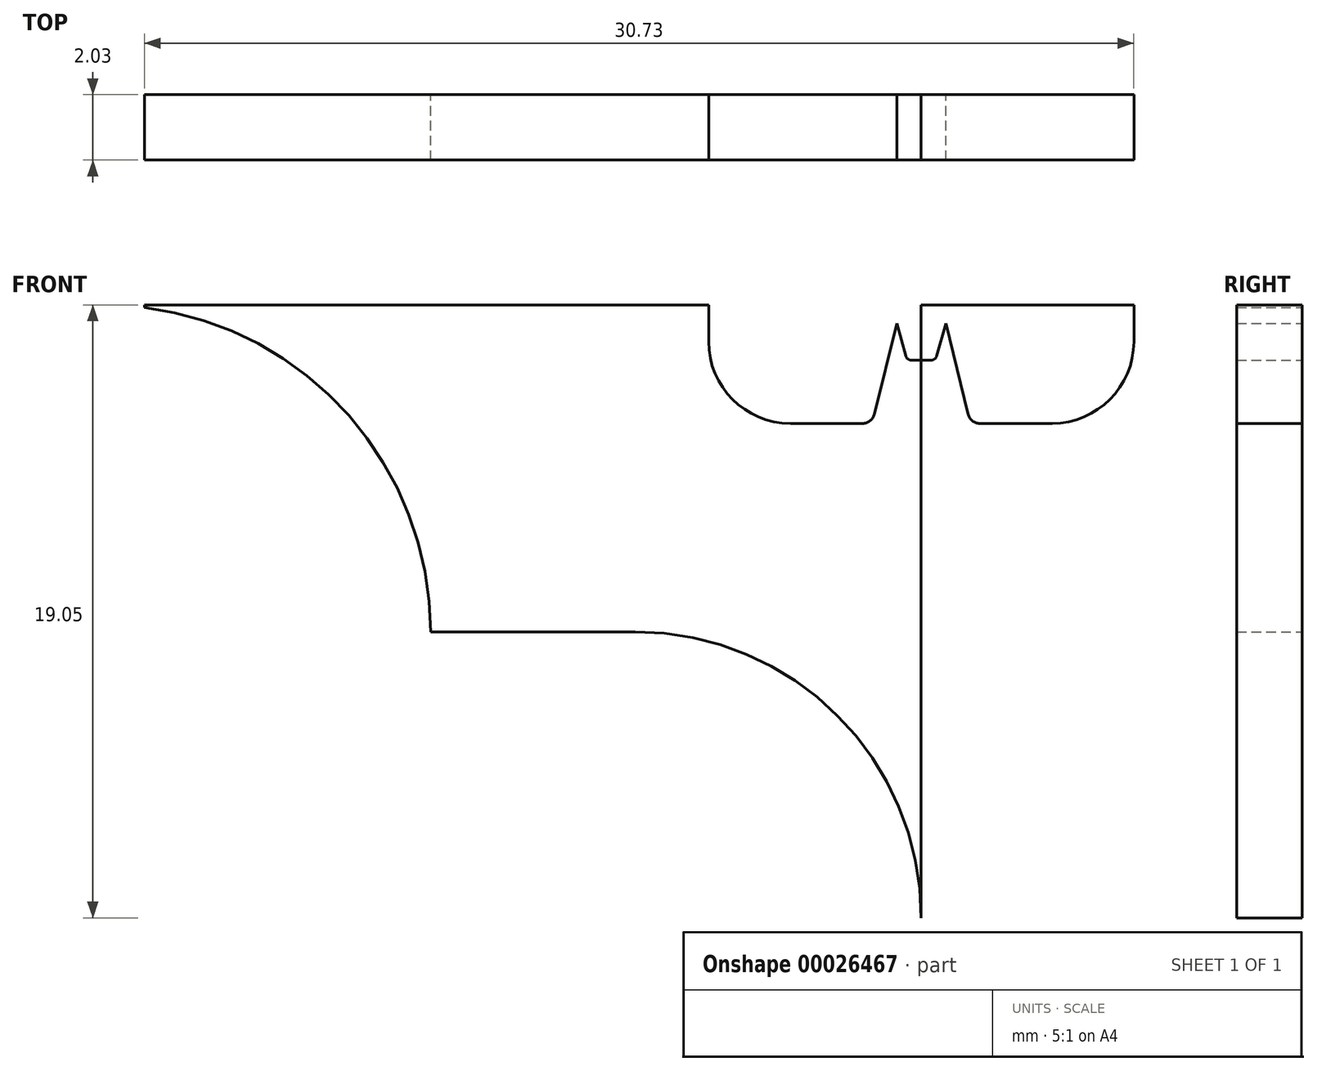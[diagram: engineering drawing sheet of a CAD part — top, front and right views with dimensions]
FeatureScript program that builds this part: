
annotation { "Feature Type Name" : "Feature", "Feature Type Description" : "" }
export const myFeature = defineFeature(function(context is Context, id is Id, definition is map)
    precondition{}
    {
        {
            var Q0;
            Q0=qCreatedBy(makeId("Front.planeOp"),FACE);
            var sketch = newSketch(context, id + "F0", { "sketchPlane" : qUnion([Q0])});
            skLineSegment(sketch, "E0", {"start": v(0, 0) * mm, "end": v(0, 50.8) * mm});
            skLineSegment(sketch, "E1.left", {"start": v(50.8, 0) * mm, "end": v(50.8, 5.14) * mm});
            skLineSegment(sketch, "E2.top", {"start": v(0, 17.78) * mm, "end": v(-1.27, 17.78) * mm});
            skLineSegment(sketch, "E2.right", {"start": v(0, 0) * mm, "end": v(0, 17.78) * mm});
            skPoint(sketch, "E3", {"position": v(0, 7.11) * mm});
            skLineSegment(sketch, "E4", {"start": v(8.9, -1.34) * mm, "end": v(8.9, 7.62) * mm});
            skPoint(sketch, "E5.newPointA", {"position": v(8.9, 9.32) * mm});
            skArc(sketch, "E5.filletArc", {"start": v(8.9, 7.62) * mm, "mid": v(5.91, 14.8) * mm, "end": v(-1.27, 17.78) * mm});
            skLineSegment(sketch, "E6", {"start": v(8.9, 7.62) * mm, "end": v(15.24, 7.62) * mm});
            skLineSegment(sketch, "E7", {"start": v(24.13, 0) * mm, "end": v(24.13, -1.27) * mm});
            skPoint(sketch, "E8.visualSharp", {"position": v(24.13, 7.62) * mm});
            skArc(sketch, "E8.filletArc", {"start": v(24.13, -1.27) * mm, "mid": v(21.53, 5.02) * mm, "end": v(15.24, 7.62) * mm});
            skLineSegment(sketch, "E9", {"start": v(-1.27, 17.78) * mm, "end": v(24.13, 17.78) * mm});
            skLineSegment(sketch, "E10", {"start": v(24.13, -1.27) * mm, "end": v(24.13, 17.78) * mm});
            skLineSegment(sketch, "E11.bottom", {"start": v(24.13, 17.78) * mm, "end": v(17.53, 17.78) * mm});
            skLineSegment(sketch, "E11.top", {"start": v(22.3, 14.1) * mm, "end": v(20.07, 14.1) * mm});
            skLineSegment(sketch, "E11.left", {"start": v(24.13, 17.78) * mm, "end": v(24.13, 14.1) * mm});
            skLineSegment(sketch, "E11.right", {"start": v(17.53, 17.78) * mm, "end": v(17.53, 16.64) * mm});
            skPoint(sketch, "E12.visualSharp", {"position": v(17.53, 14.1) * mm});
            skArc(sketch, "E12.filletArc", {"start": v(17.53, 16.64) * mm, "mid": v(18.27, 14.84) * mm, "end": v(20.07, 14.1) * mm});
            skLineSegment(sketch, "E13.bottom", {"start": v(24.13, 14.1) * mm, "end": v(22.6, 14.1) * mm});
            skLineSegment(sketch, "E13.top", {"start": v(24.13, 17.2) * mm, "end": v(22.6, 17.2) * mm, "construction": true});
            skLineSegment(sketch, "E13.left", {"start": v(24.13, 14.1) * mm, "end": v(24.13, 17.2) * mm});
            skLineSegment(sketch, "E13.right", {"start": v(22.6, 14.1) * mm, "end": v(22.6, 17.2) * mm, "construction": true});
            skLineSegment(sketch, "E14", {"start": v(22.68, 14.39) * mm, "end": v(23.37, 17.2) * mm});
            skLineSegment(sketch, "E15", {"start": v(23.37, 17.2) * mm, "end": v(23.65, 16.19) * mm});
            skLineSegment(sketch, "E16", {"start": v(23.82, 16.06) * mm, "end": v(24.13, 16.06) * mm});
            skPoint(sketch, "E17.newPointB", {"position": v(24.13, 14.1) * mm});
            skArc(sketch, "E17.filletArc", {"start": v(22.3, 14.1) * mm, "mid": v(22.54, 14.18) * mm, "end": v(22.68, 14.39) * mm});
            skPoint(sketch, "E18.visualSharp", {"position": v(23.69, 16.06) * mm});
            skArc(sketch, "E18.filletArc", {"start": v(23.65, 16.19) * mm, "mid": v(23.71, 16.1) * mm, "end": v(23.82, 16.06) * mm});
            skArc(sketch, "E19.MirrorCS", {"start": v(25.95, 14.1) * mm, "mid": v(25.72, 14.18) * mm, "end": v(25.58, 14.39) * mm});
            skLineSegment(sketch, "E20.MirrorCS", {"start": v(48.26, 17.78) * mm, "end": v(49.53, 17.78) * mm});
            skPoint(sketch, "E21.MirrorP", {"position": v(30.73, 14.1) * mm});
            skArc(sketch, "E22.MirrorCS", {"start": v(30.73, 16.64) * mm, "mid": v(30, 14.84) * mm, "end": v(28.2, 14.1) * mm});
            skLineSegment(sketch, "E23.MirrorCS", {"start": v(24.9, 17.2) * mm, "end": v(24.6, 16.19) * mm});
            skArc(sketch, "E24.MirrorCS", {"start": v(39.37, 7.62) * mm, "mid": v(42.35, 14.8) * mm, "end": v(49.53, 17.78) * mm});
            skLineSegment(sketch, "E25.MirrorCS", {"start": v(25.95, 14.1) * mm, "end": v(28.2, 14.1) * mm});
            skPoint(sketch, "E26.MirrorP", {"position": v(48.26, 7.11) * mm});
            skLineSegment(sketch, "E27.MirrorCS", {"start": v(39.37, 7.62) * mm, "end": v(33.02, 7.62) * mm});
            skLineSegment(sketch, "E28.MirrorCS", {"start": v(39.37, -1.34) * mm, "end": v(39.37, 7.62) * mm});
            skLineSegment(sketch, "E29.MirrorCS", {"start": v(25.65, 14.1) * mm, "end": v(25.65, 17.2) * mm, "construction": true});
            skLineSegment(sketch, "E30.MirrorCS", {"start": v(30.73, 17.78) * mm, "end": v(30.73, 16.64) * mm});
            skLineSegment(sketch, "E31.MirrorCS", {"start": v(25.58, 14.39) * mm, "end": v(24.9, 17.2) * mm});
            skLineSegment(sketch, "E32.MirrorCS", {"start": v(48.26, 0) * mm, "end": v(48.26, 17.78) * mm});
            skPoint(sketch, "E33.MirrorP", {"position": v(39.37, 9.32) * mm});
            skLineSegment(sketch, "E34.MirrorCS", {"start": v(24.13, 17.78) * mm, "end": v(30.73, 17.78) * mm, "construction": true});
            skArc(sketch, "E35.MirrorCS", {"start": v(24.13, -1.27) * mm, "mid": v(26.73, 5.02) * mm, "end": v(33.02, 7.62) * mm});
            skLineSegment(sketch, "E36.MirrorCS", {"start": v(49.53, 17.78) * mm, "end": v(24.13, 17.78) * mm});
            skArc(sketch, "E37.MirrorCS", {"start": v(24.6, 16.19) * mm, "mid": v(24.55, 16.1) * mm, "end": v(24.44, 16.06) * mm});
            skLineSegment(sketch, "E38.MirrorCS", {"start": v(24.44, 16.06) * mm, "end": v(24.13, 16.06) * mm});
            skPoint(sketch, "E39.MirrorP", {"position": v(24.57, 16.06) * mm});
            skLineSegment(sketch, "E40.MirrorCS", {"start": v(24.13, 17.2) * mm, "end": v(25.65, 17.2) * mm, "construction": true});
            skCircle(sketch, "E41", {"center": v(36.7, 14.04) * mm, "radius": 2.54 * mm});
            skArc(sketch, "E42.trimOffspring", {"start": v(48.26, 5.14) * mm, "mid": v(49.53, 5.08) * mm, "end": v(50.8, 5.14) * mm});
            skSolve(sketch);
        }
        {
            var Q0;
            {var subQ10=sQuery(id+"F0.wireOp",EDGE,"E6");Q0=makeQuery(id+"F0.imprint","IMPRINT",FACE,{"disambiguationData":[TD([[makeQuery(id+"F0.imprint","IMPRINT",EDGE,{"derivedFrom":subQ10}),1.0]])]});}
            var Q1;
            Q1=makeQuery(id+"F0.imprint","IMPRINT",FACE,{"disambiguationData":[TD([[makeQuery(id+"F0.imprint","IMPRINT",EDGE,{"derivedFrom":sQuery(id+"F0.wireOp",EDGE,"E19.MirrorCS")}),1.0]])]});
            extrude(context, id + "F1", {"entities" : qUnion([Q0, Q1]), "depth" : 2.03 * mm});
        }
    });
